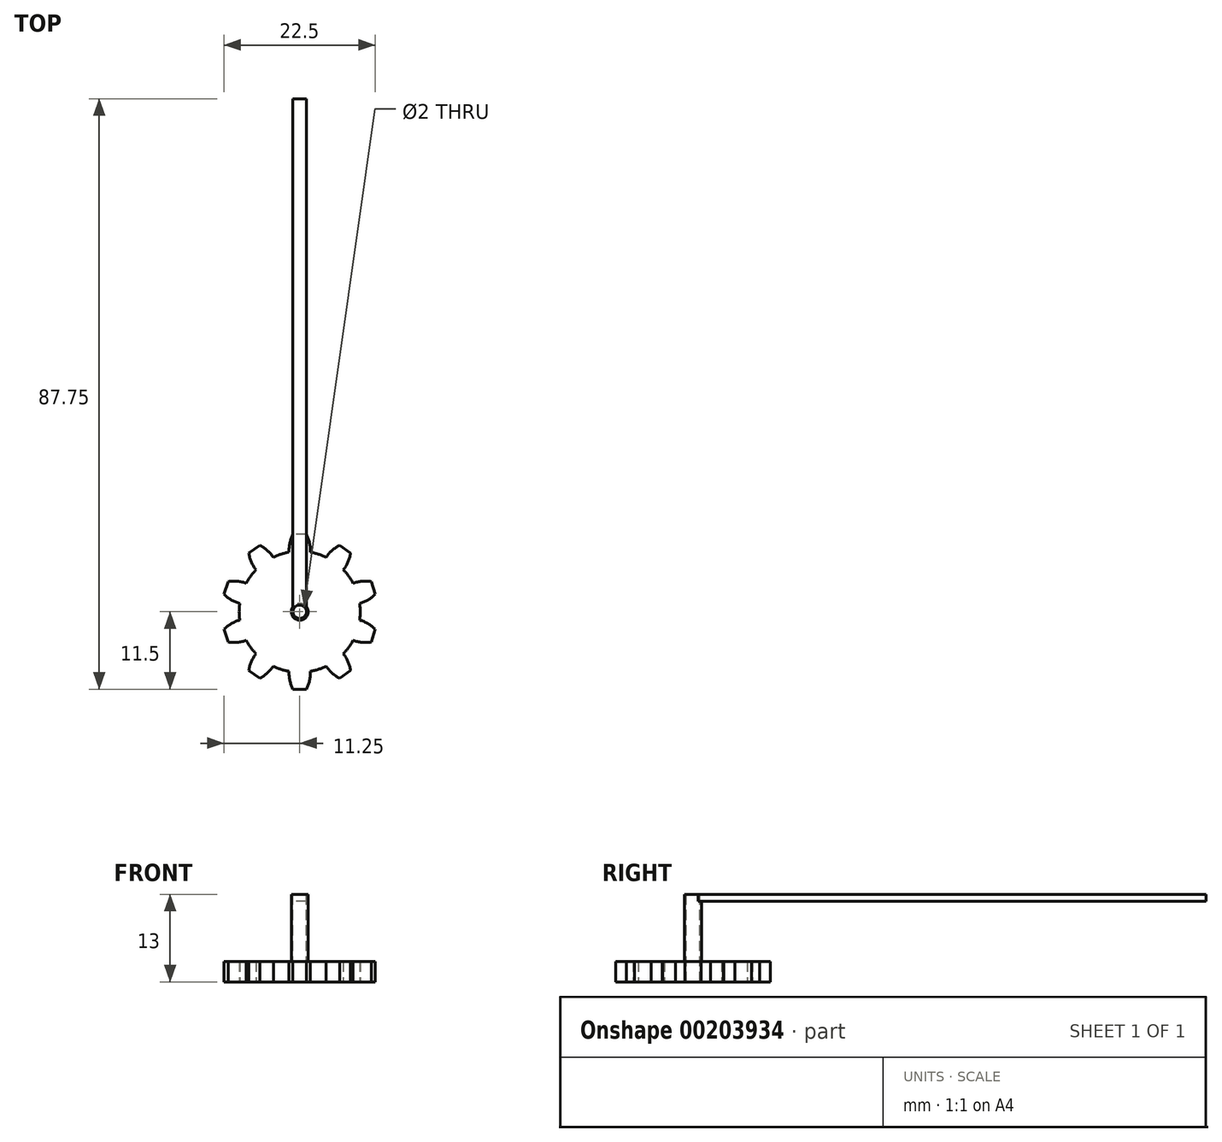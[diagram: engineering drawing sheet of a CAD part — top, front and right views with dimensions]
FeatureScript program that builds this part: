
annotation { "Feature Type Name" : "Feature", "Feature Type Description" : "" }
export const myFeature = defineFeature(function(context is Context, id is Id, definition is map)
    precondition{}
    {
        {
            var Q0;
            Q0=qCreatedBy(makeId("Top.planeOp"),FACE);
            var sketch = newSketch(context, id + "F0", { "sketchPlane" : qUnion([Q0])});
            skCircle(sketch, "E0", {"center": v(0, 0) * mm, "radius": 9 * mm});
            skLineSegment(sketch, "E1", {"start": v(0, 0) * mm, "end": v(0, 9) * mm, "construction": true});
            skLineSegment(sketch, "E2", {"start": v(0, 11.5) * mm, "end": v(-1, 11.5) * mm});
            skArc(sketch, "E3", {"start": v(-1, 11.5) * mm, "mid": v(-1.46, 10.22) * mm, "end": v(-1.59, 8.86) * mm});
            skLineSegment(sketch, "E4.MirrorCS", {"start": v(0, 11.5) * mm, "end": v(1, 11.5) * mm});
            skArc(sketch, "E5.MirrorCS", {"start": v(1, 11.5) * mm, "mid": v(1.46, 10.22) * mm, "end": v(1.59, 8.86) * mm});
            skArc(sketch, "E6.1.0", {"start": v(-7.57, 8.72) * mm, "mid": v(-7.18, 7.4) * mm, "end": v(-6.5, 6.23) * mm});
            skLineSegment(sketch, "E6.1.1", {"start": v(-6.76, 9.3) * mm, "end": v(-7.57, 8.72) * mm});
            skLineSegment(sketch, "E6.1.2", {"start": v(-6.76, 9.3) * mm, "end": v(-5.95, 9.9) * mm});
            skArc(sketch, "E6.1.3", {"start": v(-5.95, 9.9) * mm, "mid": v(-4.83, 9.12) * mm, "end": v(-3.92, 8.1) * mm});
            skArc(sketch, "E6.2.0", {"start": v(-11.25, 2.6) * mm, "mid": v(-10.17, 1.77) * mm, "end": v(-8.92, 1.23) * mm});
            skLineSegment(sketch, "E6.2.1", {"start": v(-10.94, 3.55) * mm, "end": v(-11.25, 2.6) * mm});
            skLineSegment(sketch, "E6.2.2", {"start": v(-10.94, 3.55) * mm, "end": v(-10.63, 4.5) * mm});
            skArc(sketch, "E6.2.3", {"start": v(-10.63, 4.5) * mm, "mid": v(-9.27, 4.54) * mm, "end": v(-7.93, 4.25) * mm});
            skArc(sketch, "E6.3.0", {"start": v(-10.63, -4.5) * mm, "mid": v(-9.27, -4.54) * mm, "end": v(-7.93, -4.25) * mm});
            skLineSegment(sketch, "E6.3.1", {"start": v(-10.94, -3.55) * mm, "end": v(-10.63, -4.5) * mm});
            skLineSegment(sketch, "E6.3.2", {"start": v(-10.94, -3.55) * mm, "end": v(-11.25, -2.6) * mm});
            skArc(sketch, "E6.3.3", {"start": v(-11.25, -2.6) * mm, "mid": v(-10.17, -1.77) * mm, "end": v(-8.92, -1.23) * mm});
            skArc(sketch, "E6.4.0", {"start": v(-5.95, -9.9) * mm, "mid": v(-4.83, -9.12) * mm, "end": v(-3.92, -8.1) * mm});
            skLineSegment(sketch, "E6.4.1", {"start": v(-6.76, -9.3) * mm, "end": v(-5.95, -9.9) * mm});
            skLineSegment(sketch, "E6.4.2", {"start": v(-6.76, -9.3) * mm, "end": v(-7.57, -8.72) * mm});
            skArc(sketch, "E6.4.3", {"start": v(-7.57, -8.72) * mm, "mid": v(-7.18, -7.4) * mm, "end": v(-6.5, -6.23) * mm});
            skArc(sketch, "E6.5.0", {"start": v(1, -11.5) * mm, "mid": v(1.46, -10.22) * mm, "end": v(1.59, -8.86) * mm});
            skLineSegment(sketch, "E6.5.1", {"start": v(0, -11.5) * mm, "end": v(1, -11.5) * mm});
            skLineSegment(sketch, "E6.5.2", {"start": v(0, -11.5) * mm, "end": v(-1, -11.5) * mm});
            skArc(sketch, "E6.5.3", {"start": v(-1, -11.5) * mm, "mid": v(-1.46, -10.22) * mm, "end": v(-1.59, -8.86) * mm});
            skArc(sketch, "E7.3.6.0", {"start": v(7.57, -8.72) * mm, "mid": v(7.18, -7.4) * mm, "end": v(6.5, -6.23) * mm});
            skLineSegment(sketch, "E7.4.6.0", {"start": v(6.76, -9.3) * mm, "end": v(7.57, -8.72) * mm});
            skLineSegment(sketch, "E7.7.6.0", {"start": v(6.76, -9.3) * mm, "end": v(5.95, -9.9) * mm});
            skArc(sketch, "E7.10.6.0", {"start": v(5.95, -9.9) * mm, "mid": v(4.83, -9.12) * mm, "end": v(3.92, -8.1) * mm});
            skArc(sketch, "E7.3.7.0", {"start": v(11.25, -2.6) * mm, "mid": v(10.17, -1.77) * mm, "end": v(8.92, -1.23) * mm});
            skLineSegment(sketch, "E7.4.7.0", {"start": v(10.94, -3.55) * mm, "end": v(11.25, -2.6) * mm});
            skLineSegment(sketch, "E7.7.7.0", {"start": v(10.94, -3.55) * mm, "end": v(10.63, -4.5) * mm});
            skArc(sketch, "E7.10.7.0", {"start": v(10.63, -4.5) * mm, "mid": v(9.27, -4.54) * mm, "end": v(7.93, -4.25) * mm});
            skArc(sketch, "E7.3.8.0", {"start": v(10.63, 4.5) * mm, "mid": v(9.27, 4.54) * mm, "end": v(7.93, 4.25) * mm});
            skLineSegment(sketch, "E7.4.8.0", {"start": v(10.94, 3.55) * mm, "end": v(10.63, 4.5) * mm});
            skLineSegment(sketch, "E7.7.8.0", {"start": v(10.94, 3.55) * mm, "end": v(11.25, 2.6) * mm});
            skArc(sketch, "E7.10.8.0", {"start": v(11.25, 2.6) * mm, "mid": v(10.17, 1.77) * mm, "end": v(8.92, 1.23) * mm});
            skArc(sketch, "E7.3.9.0", {"start": v(5.95, 9.9) * mm, "mid": v(4.83, 9.12) * mm, "end": v(3.92, 8.1) * mm});
            skLineSegment(sketch, "E7.4.9.0", {"start": v(6.76, 9.3) * mm, "end": v(5.95, 9.9) * mm});
            skLineSegment(sketch, "E7.7.9.0", {"start": v(6.76, 9.3) * mm, "end": v(7.57, 8.72) * mm});
            skArc(sketch, "E7.10.9.0", {"start": v(7.57, 8.72) * mm, "mid": v(7.18, 7.4) * mm, "end": v(6.5, 6.23) * mm});
            skSolve(sketch);
        }
        {
            var Q0;
            Q0=qSketchRegion(id+"F0",true);
            extrude(context, id + "F1", {"entities" : qUnion([Q0]), "depth" : 3 * mm});
        }
        {
            var Q0;
            Q0=makeQuery(id+"F1.opExtrude","CAP_FACE",FACE,{"disambiguationData":[OSD([sQuery(id+"F0.wireOp",EDGE,"E0"),sQuery(id+"F0.wireOp",EDGE,"E2"),sQuery(id+"F0.wireOp",EDGE,"E3"),sQuery(id+"F0.wireOp",EDGE,"E4.MirrorCS"),sQuery(id+"F0.wireOp",EDGE,"E5.MirrorCS"),sQuery(id+"F0.wireOp",EDGE,"E6.1.0"),sQuery(id+"F0.wireOp",EDGE,"E6.1.1"),sQuery(id+"F0.wireOp",EDGE,"E6.1.2"),sQuery(id+"F0.wireOp",EDGE,"E6.1.3"),sQuery(id+"F0.wireOp",EDGE,"E6.2.0"),sQuery(id+"F0.wireOp",EDGE,"E6.2.1"),sQuery(id+"F0.wireOp",EDGE,"E6.2.2"),sQuery(id+"F0.wireOp",EDGE,"E6.2.3"),sQuery(id+"F0.wireOp",EDGE,"E6.3.0"),sQuery(id+"F0.wireOp",EDGE,"E6.3.1"),sQuery(id+"F0.wireOp",EDGE,"E6.3.2"),sQuery(id+"F0.wireOp",EDGE,"E6.3.3"),sQuery(id+"F0.wireOp",EDGE,"E6.4.0"),sQuery(id+"F0.wireOp",EDGE,"E6.4.1"),sQuery(id+"F0.wireOp",EDGE,"E6.4.2"),sQuery(id+"F0.wireOp",EDGE,"E6.4.3"),sQuery(id+"F0.wireOp",EDGE,"E6.5.0"),sQuery(id+"F0.wireOp",EDGE,"E6.5.1"),sQuery(id+"F0.wireOp",EDGE,"E6.5.2"),sQuery(id+"F0.wireOp",EDGE,"E6.5.3"),sQuery(id+"F0.wireOp",EDGE,"E6.6.0"),sQuery(id+"F0.wireOp",EDGE,"E6.6.1"),sQuery(id+"F0.wireOp",EDGE,"E6.6.2"),sQuery(id+"F0.wireOp",EDGE,"E6.6.3"),sQuery(id+"F0.wireOp",EDGE,"E6.7.0"),sQuery(id+"F0.wireOp",EDGE,"E6.7.1"),sQuery(id+"F0.wireOp",EDGE,"E6.7.2"),sQuery(id+"F0.wireOp",EDGE,"E6.7.3"),sQuery(id+"F0.wireOp",EDGE,"E6.8.0"),sQuery(id+"F0.wireOp",EDGE,"E6.8.1"),sQuery(id+"F0.wireOp",EDGE,"E6.8.2"),sQuery(id+"F0.wireOp",EDGE,"E6.8.3"),sQuery(id+"F0.wireOp",EDGE,"E6.9.0"),sQuery(id+"F0.wireOp",EDGE,"E6.9.1"),sQuery(id+"F0.wireOp",EDGE,"E6.9.2"),sQuery(id+"F0.wireOp",EDGE,"E6.9.3"),sQuery(id+"F0.wireOp",EDGE,"E6.10.0"),sQuery(id+"F0.wireOp",EDGE,"E6.10.1"),sQuery(id+"F0.wireOp",EDGE,"E6.10.2"),sQuery(id+"F0.wireOp",EDGE,"E6.10.3"),sQuery(id+"F0.wireOp",EDGE,"E6.11.0"),sQuery(id+"F0.wireOp",EDGE,"E6.11.1"),sQuery(id+"F0.wireOp",EDGE,"E6.11.2"),sQuery(id+"F0.wireOp",EDGE,"E6.11.3"),sQuery(id+"F0.wireOp",EDGE,"E6.12.0"),sQuery(id+"F0.wireOp",EDGE,"E6.12.1"),sQuery(id+"F0.wireOp",EDGE,"E6.12.2"),sQuery(id+"F0.wireOp",EDGE,"E6.12.3"),sQuery(id+"F0.wireOp",EDGE,"E6.13.0"),sQuery(id+"F0.wireOp",EDGE,"E6.13.1"),sQuery(id+"F0.wireOp",EDGE,"E6.13.2"),sQuery(id+"F0.wireOp",EDGE,"E6.13.3"),sQuery(id+"F0.wireOp",EDGE,"E6.14.0"),sQuery(id+"F0.wireOp",EDGE,"E6.14.1"),sQuery(id+"F0.wireOp",EDGE,"E6.14.2"),sQuery(id+"F0.wireOp",EDGE,"E6.14.3"),sQuery(id+"F0.wireOp",EDGE,"E6.15.0"),sQuery(id+"F0.wireOp",EDGE,"E6.15.1"),sQuery(id+"F0.wireOp",EDGE,"E6.15.2"),sQuery(id+"F0.wireOp",EDGE,"E6.15.3")])],"isStart":false});
            var sketch = newSketch(context, id + "F2", { "sketchPlane" : qUnion([Q0])});
            skCircle(sketch, "E8", {"center": v(0, 0) * mm, "radius": 1.25 * mm});
            skSolve(sketch);
        }
        {
            var Q0;
            Q0=qSketchRegion(id+"F2",true);
            extrude(context, id + "F3", {"entities" : qUnion([Q0]), "operationType" : NewBodyOperationType.ADD, "depth" : 10 * mm});
        }
        {
            var Q0;
            Q0=makeQuery(id+"F3.opExtrude","CAP_FACE",FACE,{"disambiguationData":[OSD([sQuery(id+"F2.wireOp",EDGE,"E8")])],"isStart":false});
            var sketch = newSketch(context, id + "F4", { "sketchPlane" : qUnion([Q0])});
            skCircle(sketch, "E9", {"center": v(0, 0) * mm, "radius": 1 * mm});
            skSolve(sketch);
        }
        {
            var Q0;
            Q0=qSketchRegion(id+"F4",true);
            extrude(context, id + "F5", {"entities" : qUnion([Q0]), "operationType" : NewBodyOperationType.REMOVE, "oppositeDirection" : true, "depth" : 25 * mm});
        }
        {
            var Q0;
            Q0=makeQuery(id+"F3.opExtrude","CAP_FACE",FACE,{"disambiguationData":[OSD([sQuery(id+"F2.wireOp",EDGE,"E8")])],"isStart":false});
            var sketch = newSketch(context, id + "F6", { "sketchPlane" : qUnion([Q0])});
            skLineSegment(sketch, "E10.bottom", {"start": v(0, 1.25) * mm, "end": v(-1, 1.25) * mm});
            skLineSegment(sketch, "E10.top", {"start": v(0, 76.25) * mm, "end": v(-1, 76.25) * mm});
            skLineSegment(sketch, "E10.left", {"start": v(0, 1.25) * mm, "end": v(0, 76.25) * mm});
            skLineSegment(sketch, "E10.right", {"start": v(-1, 1.25) * mm, "end": v(-1, 76.25) * mm});
            skLineSegment(sketch, "E11.MirrorCS", {"start": v(1, 1.25) * mm, "end": v(1, 76.25) * mm});
            skLineSegment(sketch, "E12.MirrorCS", {"start": v(0, 76.25) * mm, "end": v(1, 76.25) * mm});
            skLineSegment(sketch, "E13.MirrorCS", {"start": v(0, 1.25) * mm, "end": v(1, 1.25) * mm});
            skLineSegment(sketch, "E14", {"start": v(-1, 1.25) * mm, "end": v(-1, 0.75) * mm});
            skLineSegment(sketch, "E15", {"start": v(1, 1.25) * mm, "end": v(1, 0.75) * mm});
            skArc(sketch, "E16", {"start": v(-1, 0.75) * mm, "mid": v(0, 1.25) * mm, "end": v(1, 0.75) * mm});
            skSolve(sketch);
        }
        {
            var Q0;
            Q0=qSketchRegion(id+"F6",true);
            extrude(context, id + "F7", {"entities" : qUnion([Q0]), "operationType" : NewBodyOperationType.ADD, "oppositeDirection" : true, "depth" : 1 * mm});
        }
    });
